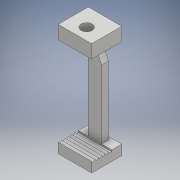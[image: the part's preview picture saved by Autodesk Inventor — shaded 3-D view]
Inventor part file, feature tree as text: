
AUTODESK INVENTOR PART (.ipt)
format: ipt  version: 2017 (Build 210142000, 142)  size: 182,784 bytes
history: native  units: mm
features: extrude x8, sketch x6, chamfer x2, projected_geometry x2
ambient origin geometry x8: Origin, YZ Plane, XZ Plane, XY Plane, X Axis, Y Axis, Z Axis, Center Point
bodies: Solid1 (feature_tree)
feature tree (18):
  extrude  "Extrusion1"  Depth=9.0mm
  extrude  "Extrusion2"  Depth=2.0mm
  sketch  "Sketch6"  dims[d5=2.0mm d6=1.5mm d7=0.0mm]
  extrude  "Extrusion5"  Depth=2.0mm TaperAngle=0.0deg
  extrude  "Extrusion6"  Depth=4.0mm TaperAngle=0.0deg
  extrude  "Extrusion7"  Depth=4.0mm
  extrude  "Extrusion10"  Depth=0.5mm
  extrude  "Extrusion11"  Depth=6.0mm
  chamfer  "Chamfer3"  Angle=135.0deg  [1 undecoded]
  chamfer  "Chamfer4"  Distance=10.0mm
  extrude  "Extrusion12"  Depth=4.0mm TaperAngle=0.0deg
  sketch  "Sketch1"  dims[d0=10.0mm d1=9.0mm]
  sketch  "Sketch2"  dims[d2=3.0mm d3=0.0mm d4=2.0mm]
  sketch  "Sketch7"  dims[d13=4.0mm d14=25.0mm d15=0.0mm]
  projected_geometry  "Projected Loop2"
  sketch  "Sketch8"  dims[d16=4.0mm d17=0.0mm d18=3.3mm]
  projected_geometry  "Projected Loop3"
  sketch  "Sketch12"  dims[d19=4.0mm d20=0.0mm d23=0.5mm d24=6.0mm d25=135.0deg d55=10.0mm d56=0.0mm d57=4.0mm d58=0.0mm d59=2.0mm d60=1.0mm d61=45.0deg d62=2.0mm d63=1.0mm d64=45.0deg d66=5.5mm d67=5.0mm d68=10.0mm d69=0.0mm]
note: 1 required parameter value undecoded (feature->parameter linkage not recoverable at this tier; creation-order binding heuristic only, values carry confidence <= 0.55)
